# Revit family: 304_Cim747H(OT)-_
name_source: partatom
category: Pipe Accessories
revit_build: Autodesk Revit 2017 (Build: 20160225_1515(x64)
units: mm (PartAtom-declared; Revit-internal decimal feet)

## family parameters
Always vertical = Yes
Cut with Voids When Loaded = No
Part Type = Valve - Breaks Into
Round Connector Dimension = Use Diameter
Shared = No
Work Plane-Based = No

## types (6) — shared parameters
CAT0 = Yes
Description = BALANCING VALVE - FIXED ORIFICE - PN 25 - HIGH FLOW
L2D_Min = 3048 mm
Manufacturer = Cimberio
QmdConnectorList = 301;D;302;D
URL = www.cimberio.it
magiPartTypeId = 304
magiProductFamilyId = Cim747H(OT)-*
zero-valued in all types: MC_Default_elevation

## per-type parameters (varying)
| type | CenSd_R1_6 | D | DD1 | DL | DL__ve | L2D | LL1 | LL2 | R1 | W2D | X | XX1 | Z |
| Cim747H(OT)-15 | 12 mm  [stored 0.0393701 ft] | 15 mm | 17 mm | 15 mm  [stored 0.0492126 ft] | -15 mm  [stored -0.0492126 ft] | 85 mm | 43 mm | 55 mm  [stored 0.180446 ft] | 14 mm  [stored 0.0459318 ft] | 15 mm  [stored 0.0492126 ft] | 105 mm  [stored 0.344488 ft] | 112 mm | 94 mm  [stored 0.308399 ft] |
| Cim747H(OT)-50 | 31 mm | 50 mm | 55 mm  [stored 0.180446 ft] | 26 mm | -26 mm | 193 mm | 97 mm | 142 mm | 36 mm | 50 mm  [stored 0.164042 ft] | 167 mm | 177 mm | 177 mm |
| Cim747H(OT)-40 | 24 mm | 40 mm | 44 mm  [stored 0.144357 ft] | 21 mm | -21 mm | 163 mm | 82 mm | 120 mm | 28 mm  [stored 0.0918635 ft] | 40 mm  [stored 0.131234 ft] | 160 mm | 166 mm | 166 mm |
| Cim747H(OT)-32 | 22 mm  [stored 0.0721785 ft] | 32 mm | 35 mm | 21 mm | -21 mm | 144 mm | 72 mm  [stored 0.23622 ft] | 101 mm | 26 mm | 32 mm  [stored 0.104987 ft] | 120 mm | 127 mm | 127 mm |
| Cim747H(OT)-25 | 17 mm | 25 mm | 28 mm  [stored 0.0918635 ft] | 19 mm | -19 mm | 113 mm | 57 mm | 75 mm | 20 mm  [stored 0.0656168 ft] | 25 mm  [stored 0.082021 ft] | 114 mm | 123 mm | 123 mm |
| Cim747H(OT)-20 | 14 mm  [stored 0.0459318 ft] | 20 mm | 22 mm  [stored 0.0721785 ft] | 16 mm | -16 mm | 97 mm | 49 mm | 64 mm | 17 mm | 20 mm  [stored 0.0656168 ft] | 123 mm | 132 mm | 111 mm  [stored 0.364173 ft] |

note: column(s) folded — value = type name in every type: magiProductCode, magiProductId

note: [stored X ft] marks values corroborated as IEEE doubles in the binary element streams (Revit-internal decimal feet)

## geometry (parser evidence)
native form markers: Sweep x2
no freeform markers — native parametric forms only
